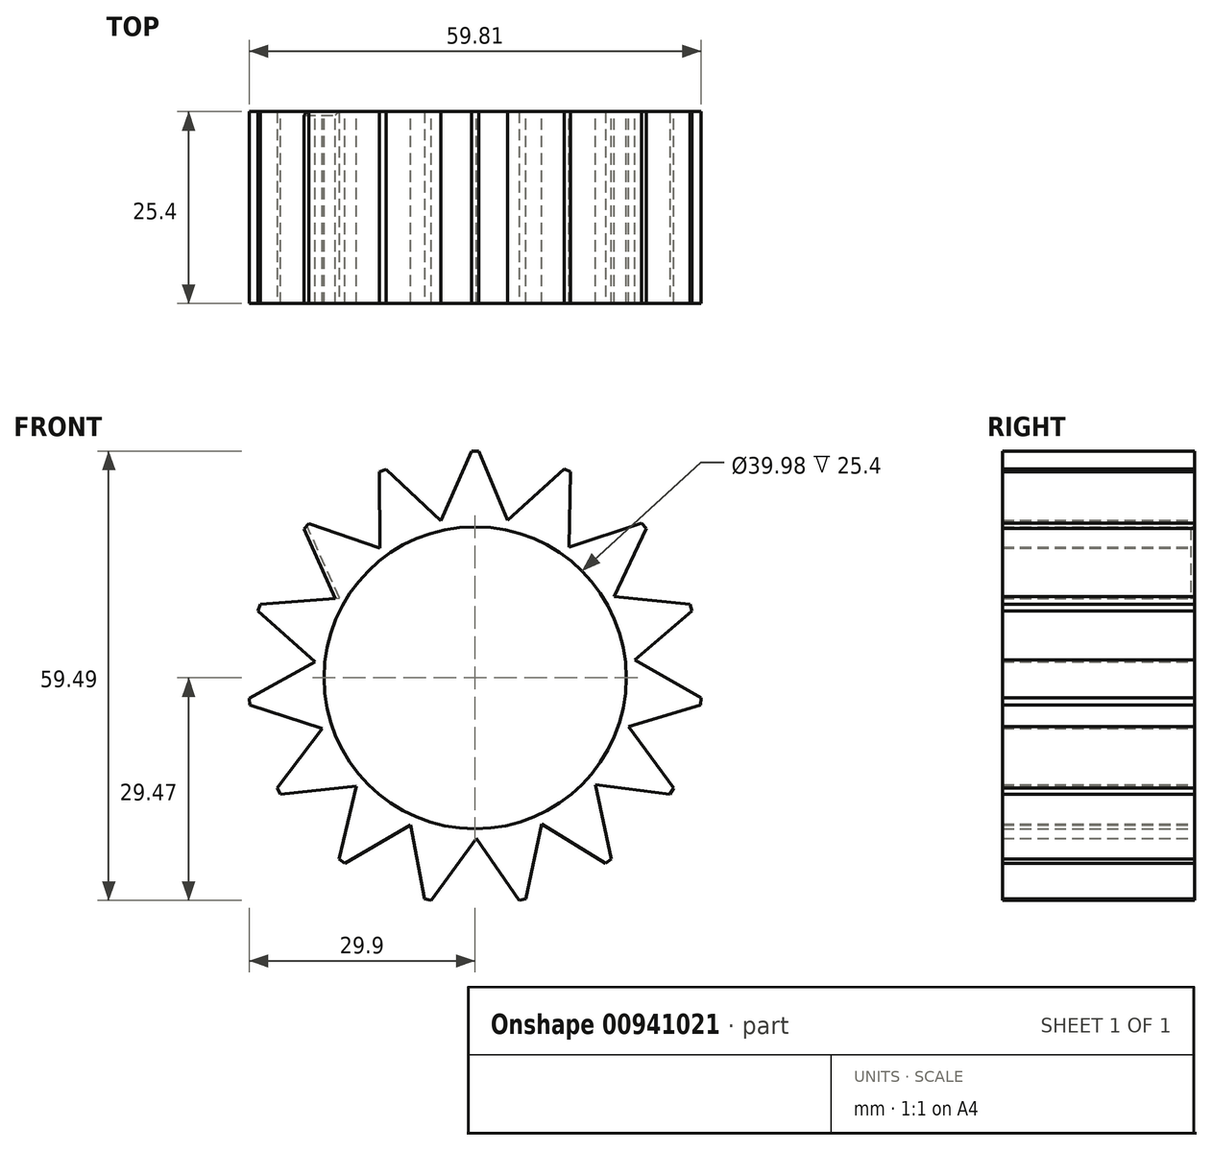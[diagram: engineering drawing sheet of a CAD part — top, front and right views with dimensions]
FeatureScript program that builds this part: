
annotation { "Feature Type Name" : "Feature", "Feature Type Description" : "" }
export const myFeature = defineFeature(function(context is Context, id is Id, definition is map)
    precondition{}
    {
        {
            var Q0;
            Q0=qCreatedBy(makeId("Front.planeOp"),FACE);
            var sketch = newSketch(context, id + "F0", { "sketchPlane" : qUnion([Q0])});
            skPoint(sketch, "E0.center", {"position": v(0, 0) * mm});
            skCircle(sketch, "E1", {"center": v(0, 0) * mm, "radius": 19.99 * mm});
            skLineSegment(sketch, "E2", {"start": v(-5.2, 19.3) * mm, "end": v(0, 31.1) * mm});
            skLineSegment(sketch, "E3", {"start": v(0, 31.1) * mm, "end": v(4.9, 19.38) * mm});
            skLineSegment(sketch, "E4.1.0", {"start": v(-12.65, 28.41) * mm, "end": v(-3.4, 19.7) * mm});
            skLineSegment(sketch, "E4.1.1", {"start": v(-12.6, 15.51) * mm, "end": v(-12.65, 28.41) * mm});
            skLineSegment(sketch, "E4.2.0", {"start": v(-23.11, 20.81) * mm, "end": v(-11.12, 16.6) * mm});
            skLineSegment(sketch, "E4.2.1", {"start": v(-17.83, 9.04) * mm, "end": v(-23.11, 20.81) * mm});
            skLineSegment(sketch, "E4.3.0", {"start": v(-29.58, 9.61) * mm, "end": v(-16.92, 10.65) * mm});
            skLineSegment(sketch, "E4.3.1", {"start": v(-19.96, 1.01) * mm, "end": v(-29.58, 9.61) * mm});
            skLineSegment(sketch, "E4.4.0", {"start": v(-30.93, -3.25) * mm, "end": v(-19.78, 2.85) * mm});
            skLineSegment(sketch, "E4.4.1", {"start": v(-18.65, -7.2) * mm, "end": v(-30.93, -3.25) * mm});
            skLineSegment(sketch, "E4.5.0", {"start": v(-26.94, -15.55) * mm, "end": v(-19.23, -5.44) * mm});
            skLineSegment(sketch, "E4.5.1", {"start": v(-14.1, -14.16) * mm, "end": v(-26.94, -15.55) * mm});
            skLineSegment(sketch, "E4.6.0", {"start": v(-18.28, -25.16) * mm, "end": v(-15.36, -12.8) * mm});
            skLineSegment(sketch, "E4.6.1", {"start": v(-7.13, -18.67) * mm, "end": v(-18.28, -25.16) * mm});
            skLineSegment(sketch, "E4.7.0", {"start": v(-6.47, -30.42) * mm, "end": v(-8.82, -17.94) * mm});
            skLineSegment(sketch, "E4.7.1", {"start": v(1.08, -19.96) * mm, "end": v(-6.47, -30.42) * mm});
            skLineSegment(sketch, "E4.8.0", {"start": v(6.47, -30.42) * mm, "end": v(-0.77, -19.97) * mm});
            skLineSegment(sketch, "E4.8.1", {"start": v(9.1, -17.8) * mm, "end": v(6.47, -30.42) * mm});
            skLineSegment(sketch, "E4.9.0", {"start": v(18.28, -25.16) * mm, "end": v(7.42, -18.56) * mm});
            skLineSegment(sketch, "E4.9.1", {"start": v(15.56, -12.55) * mm, "end": v(18.28, -25.16) * mm});
            skLineSegment(sketch, "E4.10.0", {"start": v(26.94, -15.55) * mm, "end": v(14.33, -13.93) * mm});
            skLineSegment(sketch, "E4.10.1", {"start": v(19.32, -5.14) * mm, "end": v(26.94, -15.55) * mm});
            skLineSegment(sketch, "E4.11.0", {"start": v(30.93, -3.25) * mm, "end": v(18.76, -6.9) * mm});
            skLineSegment(sketch, "E4.11.1", {"start": v(19.74, 3.16) * mm, "end": v(30.93, -3.25) * mm});
            skLineSegment(sketch, "E4.12.0", {"start": v(29.58, 9.61) * mm, "end": v(19.94, 1.33) * mm});
            skLineSegment(sketch, "E4.12.1", {"start": v(16.74, 10.92) * mm, "end": v(29.58, 9.61) * mm});
            skLineSegment(sketch, "E4.13.0", {"start": v(23.11, 20.81) * mm, "end": v(17.68, 9.32) * mm});
            skLineSegment(sketch, "E4.13.1", {"start": v(10.86, 16.78) * mm, "end": v(23.11, 20.81) * mm});
            skLineSegment(sketch, "E4.14.0", {"start": v(12.65, 28.41) * mm, "end": v(12.36, 15.7) * mm});
            skLineSegment(sketch, "E4.14.1", {"start": v(3.1, 19.75) * mm, "end": v(12.65, 28.41) * mm});
            skSolve(sketch);
        }
        {
            var Q0;
            Q0 = qSketchRegion(id + "F0", true);
            extrude(context, id + "F1", {"entities" : qUnion([Q0]), "depth" : 25.4 * mm, "offsetDistance" : 25.4 * mm});
        }
        {
            var Q0;
            Q0=makeQuery(id+"F1.opExtrude","SWEPT_EDGE",EDGE,{"disambiguationData":[OSD([sQuery(id+"F0.wireOp",EDGE,"E4.14.0"),sQuery(id+"F0.wireOp",EDGE,"E4.14.1")])]});
            var Q1;
            Q1=makeQuery(id+"F1.opExtrude","SWEPT_EDGE",EDGE,{"disambiguationData":[OSD([sQuery(id+"F0.wireOp",EDGE,"E4.13.0"),sQuery(id+"F0.wireOp",EDGE,"E4.13.1")])]});
            var Q2;
            Q2=makeQuery(id+"F1.opExtrude","SWEPT_EDGE",EDGE,{"disambiguationData":[OSD([sQuery(id+"F0.wireOp",EDGE,"E4.12.0"),sQuery(id+"F0.wireOp",EDGE,"E4.12.1")])]});
            var Q3;
            Q3=makeQuery(id+"F1.opExtrude","SWEPT_EDGE",EDGE,{"disambiguationData":[OSD([sQuery(id+"F0.wireOp",EDGE,"E4.11.0"),sQuery(id+"F0.wireOp",EDGE,"E4.11.1")])]});
            var Q4;
            Q4=makeQuery(id+"F1.opExtrude","SWEPT_EDGE",EDGE,{"disambiguationData":[OSD([sQuery(id+"F0.wireOp",EDGE,"E4.10.0"),sQuery(id+"F0.wireOp",EDGE,"E4.10.1")])]});
            var Q5;
            Q5=makeQuery(id+"F1.opExtrude","SWEPT_EDGE",EDGE,{"disambiguationData":[OSD([sQuery(id+"F0.wireOp",EDGE,"E4.9.0"),sQuery(id+"F0.wireOp",EDGE,"E4.9.1")])]});
            var Q6;
            Q6=makeQuery(id+"F1.opExtrude","SWEPT_EDGE",EDGE,{"disambiguationData":[OSD([sQuery(id+"F0.wireOp",EDGE,"E4.8.0"),sQuery(id+"F0.wireOp",EDGE,"E4.8.1")])]});
            var Q7;
            Q7=makeQuery(id+"F1.opExtrude","SWEPT_EDGE",EDGE,{"disambiguationData":[OSD([sQuery(id+"F0.wireOp",EDGE,"E4.7.0"),sQuery(id+"F0.wireOp",EDGE,"E4.7.1")])]});
            var Q8;
            Q8=makeQuery(id+"F1.opExtrude","SWEPT_EDGE",EDGE,{"disambiguationData":[OSD([sQuery(id+"F0.wireOp",EDGE,"E4.6.0"),sQuery(id+"F0.wireOp",EDGE,"E4.6.1")])]});
            var Q9;
            Q9=makeQuery(id+"F1.opExtrude","SWEPT_EDGE",EDGE,{"disambiguationData":[OSD([sQuery(id+"F0.wireOp",EDGE,"E4.5.0"),sQuery(id+"F0.wireOp",EDGE,"E4.5.1")])]});
            var Q10;
            Q10=makeQuery(id+"F1.opExtrude","SWEPT_EDGE",EDGE,{"disambiguationData":[OSD([sQuery(id+"F0.wireOp",EDGE,"E4.4.0"),sQuery(id+"F0.wireOp",EDGE,"E4.4.1")])]});
            var Q11;
            Q11=makeQuery(id+"F1.opExtrude","SWEPT_EDGE",EDGE,{"disambiguationData":[OSD([sQuery(id+"F0.wireOp",EDGE,"E4.3.0"),sQuery(id+"F0.wireOp",EDGE,"E4.3.1")])]});
            var Q12;
            Q12=makeQuery(id+"F1.opExtrude","CAP_EDGE",EDGE,{"disambiguationData":[OSD([sQuery(id+"F0.wireOp",EDGE,"E4.2.1")])],"isStart":true});
            var Q13;
            Q13=makeQuery(id+"F1.opExtrude","SWEPT_EDGE",EDGE,{"disambiguationData":[OSD([sQuery(id+"F0.wireOp",EDGE,"E4.1.0"),sQuery(id+"F0.wireOp",EDGE,"E4.1.1")])]});
            var Q14;
            Q14=makeQuery(id+"F1.opExtrude","SWEPT_EDGE",EDGE,{"disambiguationData":[OSD([sQuery(id+"F0.wireOp",EDGE,"E4.2.0"),sQuery(id+"F0.wireOp",EDGE,"E4.2.1")])]});
            var Q15;
            Q15=makeQuery(id+"F1.opExtrude","SWEPT_EDGE",EDGE,{"disambiguationData":[OSD([sQuery(id+"F0.wireOp",EDGE,"E2"),sQuery(id+"F0.wireOp",EDGE,"E3")])]});
            chamfer(context, id + "F2", {"entities" : qUnion([Q0, Q1, Q2, Q3, Q4, Q5, Q6, Q7, Q8, Q9, Q10, Q11, Q12, Q13, Q14, Q15]), "width" : 0.5 * mm, "tangentPropagation" : true});
        }
    });
